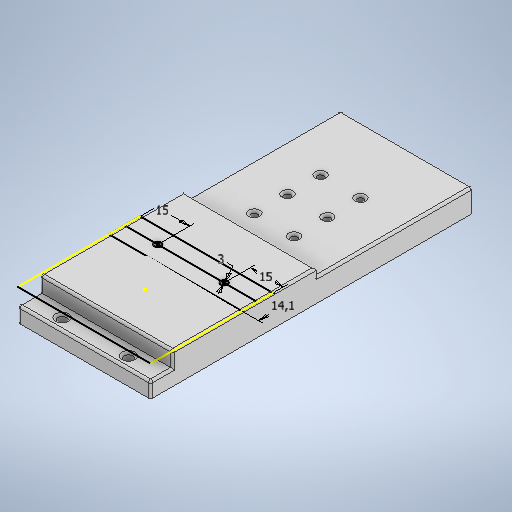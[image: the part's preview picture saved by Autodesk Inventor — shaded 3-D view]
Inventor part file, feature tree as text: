
AUTODESK INVENTOR PART (.ipt)
format: ipt  version: 2025.1 (Build 291241000, 241)  size: 457,216 bytes
history: native  units: mm
features: extrude x8, sketch x7, fillet x1
ambient origin geometry x8: Origin, YZ Plane, XZ Plane, XY Plane, X Axis, Y Axis, Z Axis, Center Point
bodies: Solide1 (feature_tree)
feature tree (16):
  extrude  "Extrusion1"  Depth=60.0mm
  sketch  "Esquisse2"
  extrude  "Extrusion2"  Depth=14.0mm TaperAngle=0.0deg
  extrude  "Extrusion4"  Depth=50.0mm TaperAngle=0.0deg
  extrude  "Extrusion5"  Depth=55.3mm
  extrude  "Extrusion6"  Depth=19.6mm TaperAngle=0.0deg
  extrude  "Extrusion8"  Depth=10.4mm
  extrude  "Extrusion9"  Depth=71.0mm TaperAngle=0.0deg
  fillet  "Congé1"  Radius=18.0mm
  extrude  "Extrusion10"  Depth=11.0mm
  sketch  "Esquisse1"
  sketch  "Esquisse5"
  sketch  "Esquisse6"
  sketch  "Esquisse7"
  sketch  "Esquisse9"
  sketch  "Esquisse10"
